# Revit family: CUBPRO_Ceiling Hosted_R16_V1.2
name_source: partatom
category: Lighting Fixtures
revit_build: Autodesk Revit 2016 (Build: 20150220_1215(x64)
units: mm (PartAtom-declared; Revit-internal decimal feet)

## family parameters
Always vertical = Yes
Cut with Voids When Loaded = No
Host = Ceiling
Light Source = Yes
OmniClass Number = 23.80.70.11
OmniClass Title = Luminaries for Internal Lighting
Part Type = Normal
Room Calculation Point = No
Round Connector Dimension = Use Diameter
Shared = No
Work Plane-Based = No

## types (3) — shared parameters
AS2293 Classification = C0=E6.3 C90=6.3
Battery Type = Lithium Iron Phosphate 3.2V 1500mAh
Ceiling = <By Category>
Ceiling Cut-out = 350 x 48mm
Charging Method = Intelligent Current Limited Constant Voltage
Color Filter = 16777215
Construction = PC Body with PC Diffuser
Diffuser = All pictograph directional inserts included in the box
Dimensions = 317 x 8.7 x 157mm (Blade), 385 x 67 (Cover Plate)
Dimming Lamp Color Temperature Shift = <None>
Emit Shape Visible in Rendering = No
Emit from Rectangle Length = 1219 mm
Emit from Rectangle Width = 610 mm
IP Rating = IP20
Lamp = 12 x Duris E3 LED, 100,000hrs
Minumum Ceiling Depth = 80mm
Mounting = Recessed Ceiling
Operating Mode = Maintained
Operating Temperature = 1 to 40C
Operating Voltage = 240V AC; 50Hz
Photometric Web File = ll21009 - CUBPRO-ZW(CT10622, Emergency).IES
Power Consumption = 1.4W (Standby), 3.7W (max)
Tilt Angle = 90.00°
Viewing Distance = 24m
Weight = 1.1kg

## per-type parameters (varying)
| type | Product Description | Testing Mode |
| CUBPRO | LP Premium Ultrablade Pro Blade Exit, Enabled with Clevertest Plus | Clevertest Plus Enabled (Not activated by default) |
| CUBPRO-DALI | LP Premium Ultrablade Pro Blade Exit | DALI Compatible |
| CUBPRO-ZW | LP Premium Ultrablade Pro Blade Exit | Zoneworks Computerised Testing |

## geometry (parser evidence)
native form markers: Sweep x3
no freeform markers — native parametric forms only
